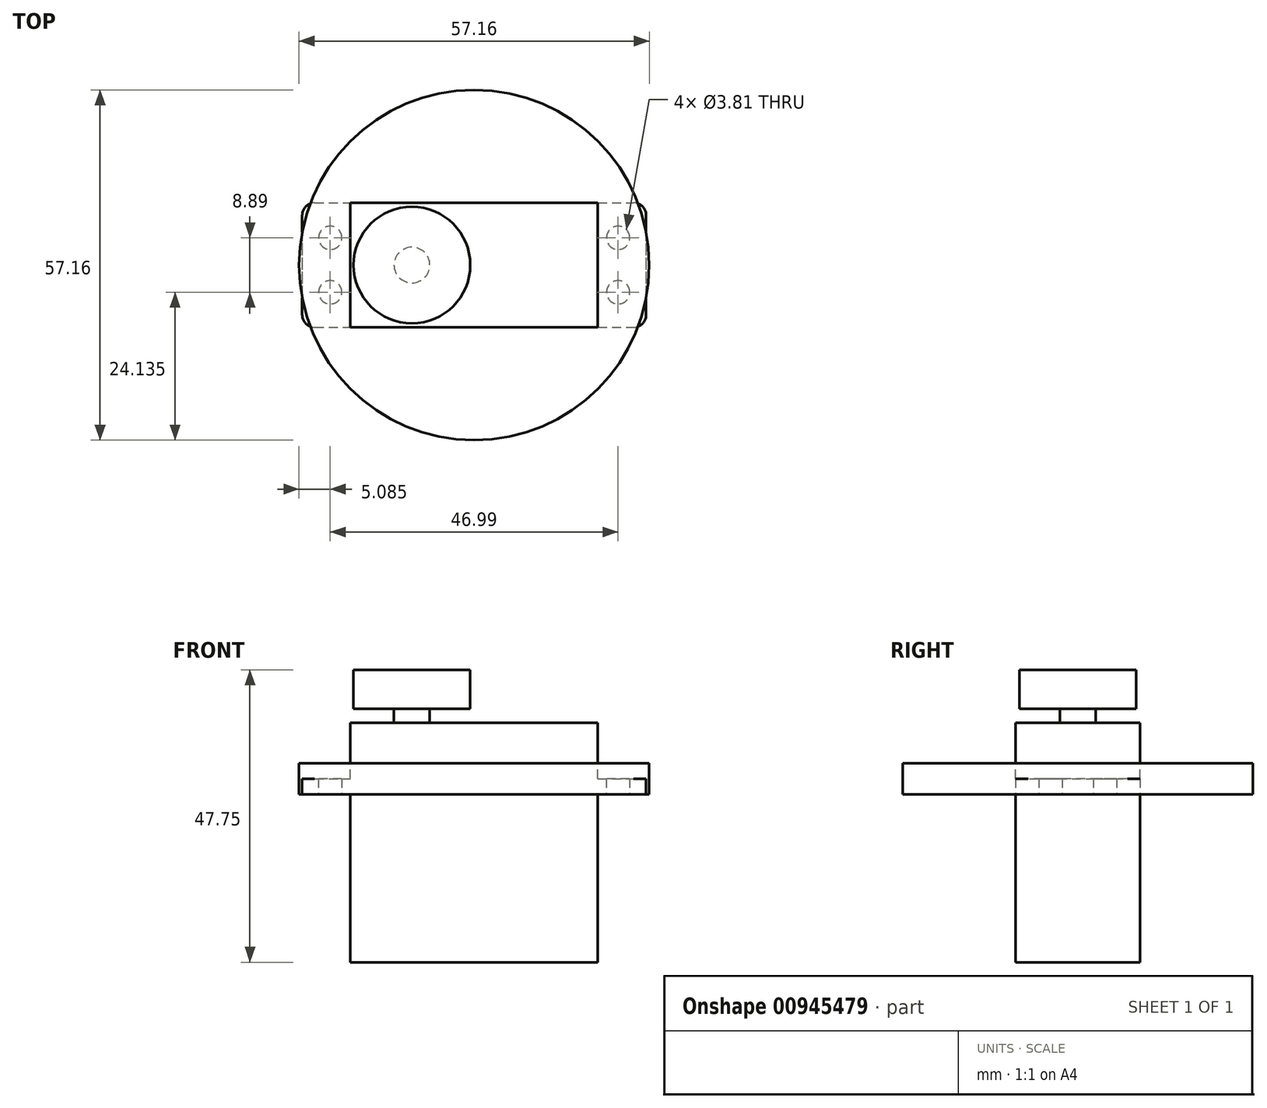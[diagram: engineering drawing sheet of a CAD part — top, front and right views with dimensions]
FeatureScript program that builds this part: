
annotation { "Feature Type Name" : "Feature", "Feature Type Description" : "" }
export const myFeature = defineFeature(function(context is Context, id is Id, definition is map)
    precondition{}
    {
        {
            var Q0;
            Q0=qCreatedBy(makeId("Top.planeOp"),FACE);
            var sketch = newSketch(context, id + "F0", { "sketchPlane" : qUnion([Q0])});
            skLineSegment(sketch, "E0.bottom", {"start": v(-20.2, 10.16) * mm, "end": v(20.2, 10.16) * mm});
            skLineSegment(sketch, "E0.top", {"start": v(-20.2, -10.16) * mm, "end": v(20.2, -10.16) * mm});
            skLineSegment(sketch, "E0.left", {"start": v(-20.2, 10.16) * mm, "end": v(-20.2, -10.16) * mm});
            skLineSegment(sketch, "E0.right", {"start": v(20.2, 10.16) * mm, "end": v(20.2, -10.16) * mm});
            skSolve(sketch);
        }
        {
            var Q0;
            Q0=qSketchRegion(id+"F0",true);
            extrude(context, id + "F1", {"entities" : qUnion([Q0]), "oppositeDirection" : true, "depth" : 27.43 * mm, "hasSecondDirection" : true, "secondDirectionOppositeDirection" : false, "secondDirectionDepth" : 11.68 * mm});
        }
        {
            var Q0;
            Q0=qCreatedBy(makeId("Top.planeOp"),FACE);
            var sketch = newSketch(context, id + "F2", { "sketchPlane" : qUnion([Q0])});
            skLineSegment(sketch, "E1.bottom", {"start": v(-26.04, 10.16) * mm, "end": v(26.04, 10.16) * mm});
            skLineSegment(sketch, "E1.top", {"start": v(-26.04, -10.16) * mm, "end": v(26.04, -10.16) * mm});
            skLineSegment(sketch, "E1.left", {"start": v(-28.07, 8.13) * mm, "end": v(-28.07, -8.13) * mm});
            skLineSegment(sketch, "E1.right", {"start": v(28.07, 8.13) * mm, "end": v(28.07, -8.13) * mm});
            skPoint(sketch, "E2.visualSharp", {"position": v(-28.07, 10.16) * mm});
            skArc(sketch, "E2.filletArc", {"start": v(-26.04, 10.16) * mm, "mid": v(-27.47, 9.56) * mm, "end": v(-28.07, 8.13) * mm});
            skPoint(sketch, "E3.visualSharp", {"position": v(-28.07, -10.16) * mm});
            skArc(sketch, "E3.filletArc", {"start": v(-28.07, -8.13) * mm, "mid": v(-27.47, -9.56) * mm, "end": v(-26.04, -10.16) * mm});
            skPoint(sketch, "E4.visualSharp", {"position": v(28.07, -10.16) * mm});
            skArc(sketch, "E4.filletArc", {"start": v(26.04, -10.16) * mm, "mid": v(27.47, -9.56) * mm, "end": v(28.07, -8.13) * mm});
            skPoint(sketch, "E5.visualSharp", {"position": v(28.07, 10.16) * mm});
            skArc(sketch, "E5.filletArc", {"start": v(28.07, 8.13) * mm, "mid": v(27.47, 9.56) * mm, "end": v(26.04, 10.16) * mm});
            skLineSegment(sketch, "E6.bottom", {"start": v(-23.5, 4.45) * mm, "end": v(23.5, 4.44) * mm, "construction": true});
            skLineSegment(sketch, "E6.top", {"start": v(-23.5, -4.44) * mm, "end": v(23.5, -4.45) * mm, "construction": true});
            skLineSegment(sketch, "E6.left", {"start": v(-23.5, 4.44) * mm, "end": v(-23.5, -4.44) * mm, "construction": true});
            skLineSegment(sketch, "E6.right", {"start": v(23.5, 4.44) * mm, "end": v(23.5, -4.44) * mm, "construction": true});
            skCircle(sketch, "E7", {"center": v(-23.5, 4.45) * mm, "radius": 1.9 * mm});
            skCircle(sketch, "E8", {"center": v(-23.5, -4.44) * mm, "radius": 1.9 * mm});
            skCircle(sketch, "E9", {"center": v(23.5, -4.45) * mm, "radius": 1.9 * mm});
            skCircle(sketch, "E10", {"center": v(23.5, 4.44) * mm, "radius": 1.9 * mm});
            skSolve(sketch);
        }
        {
            var Q0;
            Q0=qSketchRegion(id+"F2",true);
            extrude(context, id + "F3", {"entities" : qUnion([Q0]), "operationType" : NewBodyOperationType.ADD, "depth" : 2.54 * mm});
        }
        {
            var Q0;
            Q0=makeQuery(id+"F1.opExtrude","CAP_FACE",FACE,{"disambiguationData":[OSD([sQuery(id+"F0.wireOp",EDGE,"E0.bottom"),sQuery(id+"F0.wireOp",EDGE,"E0.top"),sQuery(id+"F0.wireOp",EDGE,"E0.left"),sQuery(id+"F0.wireOp",EDGE,"E0.right")])],"isStart":true});
            var sketch = newSketch(context, id + "F4", { "sketchPlane" : qUnion([Q0])});
            skCircle(sketch, "E11", {"center": v(-10.16, 0) * mm, "radius": 2.92 * mm});
            skSolve(sketch);
        }
        {
            var Q0;
            Q0=qSketchRegion(id+"F4",true);
            extrude(context, id + "F5", {"entities" : qUnion([Q0]), "operationType" : NewBodyOperationType.ADD, "depth" : 5.33 * mm});
        }
        {
            var Q0;
            Q0=makeQuery(id+"F5.opExtrude","CAP_FACE",FACE,{"disambiguationData":[OSD([sQuery(id+"F4.wireOp",EDGE,"E11")])],"isStart":false});
            var sketch = newSketch(context, id + "F6", { "sketchPlane" : qUnion([Q0])});
            skCircle(sketch, "E12", {"center": v(-10.16, 0) * mm, "radius": 9.53 * mm});
            skSolve(sketch);
        }
        {
            var Q0;
            Q0=qSketchRegion(id+"F6",true);
            extrude(context, id + "F7", {"entities" : qUnion([Q0]), "operationType" : NewBodyOperationType.ADD, "depth" : 3.3 * mm, "hasSecondDirection" : true, "secondDirectionOppositeDirection" : true, "secondDirectionDepth" : 3.05 * mm});
        }
        {
            var Q0;
            Q0=qCreatedBy(makeId("Top.planeOp"),FACE);
            var sketch = newSketch(context, id + "F8", { "sketchPlane" : qUnion([Q0])});
            skCircle(sketch, "E13", {"center": v(0, 0) * mm, "radius": 28.58 * mm});
            skSolve(sketch);
        }
        {
            var Q0;
            Q0=qSketchRegion(id+"F8",true);
            extrude(context, id + "F9", {"entities" : qUnion([Q0]), "depth" : 5.08 * mm});
        }
    });
